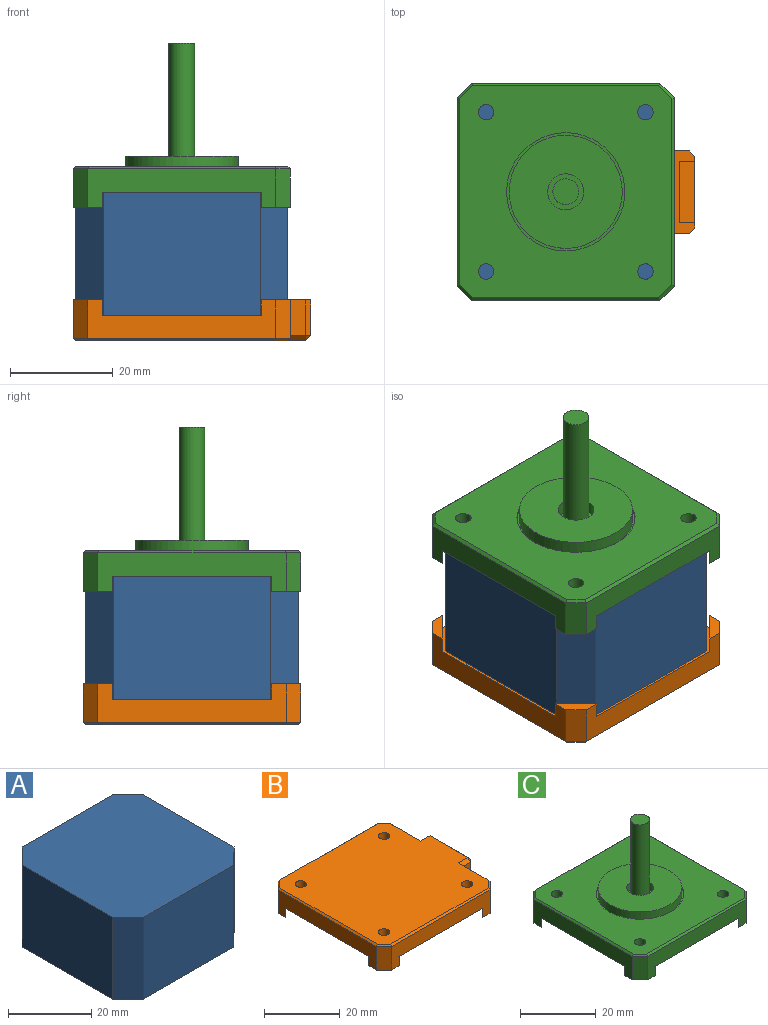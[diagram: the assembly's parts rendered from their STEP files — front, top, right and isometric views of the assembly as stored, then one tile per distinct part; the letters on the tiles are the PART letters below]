
ASSEMBLY  parts=3 mates=2
PART A: 10 faces, bbox 41.3x41.3x24 mm
  f0: plane 30.57x24mm, normal (0,1,0), area 733.7mm2, adj f1,f7,f8,f9
  f1: plane 24x5.36mm, normal (-0.71,0.71,0), area 182.1mm2, adj f0,f2,f8,f9
  f2: plane 30.57x24mm, normal (-1,0,0), area 733.7mm2, adj f1,f3,f8,f9
  f3: plane 24x5.36mm, normal (-0.71,-0.71,0), area 182.1mm2, adj f2,f4,f8,f9
  f4: plane 30.57x24mm, normal (0,-1,0), area 733.7mm2, adj f3,f5,f8,f9
  f5: plane 24x5.36mm, normal (0.71,-0.71,0), area 182.1mm2, adj f4,f6,f8,f9
  f6: plane 30.57x24mm, normal (1,0,0), area 733.7mm2, adj f5,f7,f8,f9
  f7: plane 24x5.36mm, normal (0.71,0.71,0), area 182.1mm2, adj f0,f6,f8,f9
  f8: plane 41.3x41.3mm, normal (0,0,1), area 1648.1mm2, adj f0,f1,f2,f3,f4,f5,f6,f7
  f9: plane 41.3x41.3mm, normal (0,0,-1), area 1648.1mm2, adj f0,f1,f2,f3,f4,f5,f6,f7
PART B: 48 faces, bbox 46.3x42.3x8 mm
  f0: plane 42.3x42.3mm, normal (0,0,-1), area 1697mm2, adj f1,f3,f5,f7,f9,f12,f13,f14
  f1: plane 10.82x7.5mm, normal (1,0,0), area 55.1mm2, adj f0,f2,f15,f22,f23,f32,f39
  f2: plane 7.5x2.83mm, normal (0.71,0.71,0), area 30mm2, adj f1,f3,f23,f40
  f3: plane 36.64x7.5mm, normal (0,1,0), area 181.9mm2, adj f0,f2,f4,f20,f21,f22,f23,f41
  f4: plane 7.5x2.83mm, normal (-0.71,0.71,0), area 30mm2, adj f3,f5,f21,f42
  f5: plane 36.64x7.5mm, normal (-1,0,0), area 181.9mm2, adj f0,f4,f6,f18,f19,f20,f21,f43
  f6: plane 7.5x2.83mm, normal (-0.71,-0.71,0), area 30mm2, adj f5,f7,f19,f44
  f7: plane 36.64x7.5mm, normal (0,-1,0), area 181.9mm2, adj f0,f6,f8,f18,f19,f29,f30,f45
  f8: plane 7.5x2.83mm, normal (0.71,-0.71,0), area 30mm2, adj f7,f9,f30,f46
  f9: plane 10.82x7.5mm, normal (1,0,0), area 55.1mm2, adj f0,f8,f10,f29,f30,f35,f47
  f10: plane 7x3mm, normal (0,-1,0), area 21mm2, adj f9,f25,f28,f35,f38
  f11: plane 14x7mm, normal (1,0,0), area 38mm2, adj f24,f26,f28,f31,f33,f36,f38
  f12: cylinder r=1.5mm len=5mm, axis (0,0,-1), area 47.1mm2, adj f0,f17
  f13: cylinder r=1.5mm len=5mm, axis (0,0,-1), area 47.1mm2, adj f0,f17
  f14: cylinder r=1.5mm len=5mm, axis (0,0,-1), area 47.1mm2, adj f0,f17
  f15: plane 7x3mm, normal (0,1,0), area 21mm2, adj f1,f25,f28,f32,f33
  f16: cylinder r=1.5mm len=5mm, axis (0,0,-1), area 47.1mm2, adj f0,f17
  f17: plane 44.8x41.3mm, normal (0,0,1), area 1713.6mm2, adj f12,f13,f14,f16,f32,f35,f36,f39
  f18: plane 5.66x5.66mm, normal (0.71,0.71,0), area 24mm2, adj f0,f5,f7,f19
  f19: plane 5.66x5.66mm, normal (0,0,-1), area 12mm2, adj f5,f6,f7,f18
  f20: plane 5.66x5.66mm, normal (0.71,-0.71,0), area 24mm2, adj f0,f3,f5,f21
  f21: plane 5.66x5.66mm, normal (0,0,-1), area 12mm2, adj f3,f4,f5,f20
  f22: plane 5.66x5.66mm, normal (-0.71,-0.71,0), area 24mm2, adj f0,f1,f3,f23
  f23: plane 5.66x5.66mm, normal (0,0,-1), area 12mm2, adj f1,f2,f3,f22
  f24: plane 5x3mm, normal (0,-1,0), area 15mm2, adj f11,f27,f28,f31
  f25: plane 16x3mm, normal (-1,0,0), area 48mm2, adj f0,f10,f15,f28
  f26: plane 5x3mm, normal (0,1,0), area 15mm2, adj f11,f27,f28,f31
  f27: plane 12x5mm, normal (1,0,0), area 60mm2, adj f24,f26,f28,f31
  f28: plane 16x4mm, normal (0,0,-1), area 27mm2, adj f10,f11,f15,f24,f25,f26,f27,f33
  f29: plane 5.66x5.66mm, normal (-0.71,0.71,0), area 24mm2, adj f0,f7,f9,f30
  f30: plane 5.66x5.66mm, normal (0,0,-1), area 12mm2, adj f7,f8,f9,f29
  f31: plane 12x3mm, normal (0,0,-1), area 36mm2, adj f11,f24,f26,f27
  f32: plane 3.5x1mm, normal (0,0.71,0.71), area 4.4mm2, adj f1,f15,f17,f34,f39
  f33: plane 7x1mm, normal (0.71,0.71,0), area 9.9mm2, adj f11,f15,f28,f34
  f34: plane 1x1mm, normal (0.58,0.58,0.58), area 0.9mm2, adj f32,f33,f36
  f35: plane 3.5x1mm, normal (0,-0.71,0.71), area 4.4mm2, adj f9,f10,f17,f37,f47
  f36: plane 14x1mm, normal (0.71,0,0.71), area 19.8mm2, adj f11,f17,f34,f37
  f37: plane 1x1mm, normal (0.58,-0.58,0.58), area 0.9mm2, adj f35,f36,f38
  f38: plane 7x1mm, normal (0.71,-0.71,0), area 9.9mm2, adj f10,f11,f28,f37
  f39: plane 11.32x0.5mm, normal (0.71,0,0.71), area 7.8mm2, adj f1,f17,f32,f40
  f40: plane 3.04x3.04mm, normal (0.5,0.5,0.71), area 2.7mm2, adj f2,f17,f39,f41
  f41: plane 36.64x0.5mm, normal (0,0.71,0.71), area 25.8mm2, adj f3,f17,f40,f42
  f42: plane 3.04x3.04mm, normal (-0.5,0.5,0.71), area 2.7mm2, adj f4,f17,f41,f43
  f43: plane 36.64x0.5mm, normal (-0.71,0,0.71), area 25.8mm2, adj f5,f17,f42,f44
  f44: plane 3.04x3.04mm, normal (-0.5,-0.5,0.71), area 2.7mm2, adj f6,f17,f43,f45
  f45: plane 36.64x0.5mm, normal (0,-0.71,0.71), area 25.8mm2, adj f7,f17,f44,f46
  f46: plane 3.04x3.04mm, normal (0.5,-0.5,0.71), area 2.7mm2, adj f8,f17,f45,f47
  f47: plane 11.32x0.5mm, normal (0.71,0,0.71), area 7.8mm2, adj f9,f17,f35,f46
PART C: 38 faces, bbox 42.3x42.3x32 mm
  f0: plane 36.64x7.5mm, normal (-1,0,0), area 181.9mm2, adj f1,f10,f13,f14,f15,f20,f21,f32
  f1: plane 7.5x2.83mm, normal (-0.71,-0.71,0), area 30mm2, adj f0,f2,f15,f34
  f2: plane 36.64x7.5mm, normal (0,-1,0), area 181.9mm2, adj f1,f3,f13,f14,f15,f16,f17,f36
  f3: plane 7.5x2.83mm, normal (0.71,-0.71,0), area 30mm2, adj f2,f4,f17,f37
  f4: plane 36.64x7.5mm, normal (1,0,0), area 181.9mm2, adj f3,f5,f13,f16,f17,f18,f19,f35
  f5: plane 7.5x2.83mm, normal (0.71,0.71,0), area 30mm2, adj f4,f6,f19,f33
  f6: plane 36.64x7.5mm, normal (0,1,0), area 181.9mm2, adj f5,f10,f13,f18,f19,f20,f21,f31
  f7: cylinder r=1.5mm len=5mm, axis (0,0,-1), area 47.1mm2, adj f12,f13
  f8: cylinder r=1.5mm len=5mm, axis (0,0,-1), area 47.1mm2, adj f12,f13
  f9: cylinder r=1.5mm len=5mm, axis (0,0,-1), area 47.1mm2, adj f12,f13
  f10: plane 7.5x2.83mm, normal (-0.71,0.71,0), area 30mm2, adj f0,f6,f21,f30
  f11: cylinder r=1.5mm len=5mm, axis (0,0,-1), area 47.1mm2, adj f12,f13
  f12: plane 41.3x41.3mm, normal (0,0,1), area 1249.1mm2, adj f7,f8,f9,f11,f23,f30,f31,f32
  f13: plane 42.3x42.3mm, normal (0,0,-1), area 1697mm2, adj f0,f2,f4,f6,f7,f8,f9,f11
  f14: plane 5.66x5.66mm, normal (0.71,0.71,0), area 24mm2, adj f0,f2,f13,f15
  f15: plane 5.66x5.66mm, normal (0,0,-1), area 12mm2, adj f0,f1,f2,f14
  f16: plane 5.66x5.66mm, normal (-0.71,0.71,0), area 24mm2, adj f2,f4,f13,f17
  f17: plane 5.66x5.66mm, normal (0,0,-1), area 12mm2, adj f2,f3,f4,f16
  f18: plane 5.66x5.66mm, normal (-0.71,-0.71,0), area 24mm2, adj f4,f6,f13,f19
  f19: plane 5.66x5.66mm, normal (0,0,-1), area 12mm2, adj f4,f5,f6,f18
  f20: plane 5.66x5.66mm, normal (0.71,-0.71,0), area 24mm2, adj f0,f6,f13,f21
  f21: plane 5.66x5.66mm, normal (0,0,-1), area 12mm2, adj f0,f6,f10,f20
  f22: cylinder r=11mm len=22mm, axis (0,0,-1), area 172.8mm2, adj f24,f25
  f23: cylinder r=11.5mm len=23mm, axis (0,0,-1), area 36.1mm2, adj f12,f24
  f24: plane 23x23mm, normal (0,0,1), area 35.3mm2, adj f22,f23
  f25: plane 22x22mm, normal (0,0,1), area 341.6mm2, adj f22,f27
  f26: cylinder r=2.5mm len=24.5mm, axis (0,0,-1), area 384.8mm2, adj f28,f29
  f27: cylinder r=3.5mm len=7mm, axis (0,0,-1), area 55mm2, adj f25,f28
  f28: plane 7x7mm, normal (0,0,1), area 18.8mm2, adj f26,f27
  f29: plane 5x5mm, normal (0,0,1), area 19.6mm2, adj f26
  f30: plane 3.04x3.04mm, normal (-0.5,0.5,0.71), area 2.7mm2, adj f10,f12,f31,f32
  f31: plane 36.64x0.5mm, normal (0,0.71,0.71), area 25.8mm2, adj f6,f12,f30,f33
  f32: plane 36.64x0.5mm, normal (-0.71,0,0.71), area 25.8mm2, adj f0,f12,f30,f34
  f33: plane 3.04x3.04mm, normal (0.5,0.5,0.71), area 2.7mm2, adj f5,f12,f31,f35
  f34: plane 3.04x3.04mm, normal (-0.5,-0.5,0.71), area 2.7mm2, adj f1,f12,f32,f36
  f35: plane 36.64x0.5mm, normal (0.71,0,0.71), area 25.8mm2, adj f4,f12,f33,f37
  f36: plane 36.64x0.5mm, normal (0,-0.71,0.71), area 25.8mm2, adj f2,f12,f34,f37
  f37: plane 3.04x3.04mm, normal (0.5,-0.5,0.71), area 2.7mm2, adj f3,f12,f35,f36
PLACE A t=(-62.3,-42.3,-24)mm
PLACE B rot(axis=(1,0,0),180deg) t=(0,104.6,-24)mm
PLACE C at identity fixed
MATE fastened B.f0 <-> A.f9  axis (0,0,1) through (0,0,-24)mm
MATE fastened C.f23 <-> A.f8  axis (0,0,-1) through (0,0,0)mm
